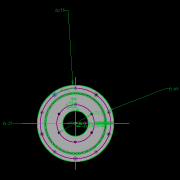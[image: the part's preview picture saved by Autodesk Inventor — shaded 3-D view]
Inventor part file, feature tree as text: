
AUTODESK INVENTOR PART (.ipt)
format: ipt  version: 2022.2 (Build 262287010, 287A)  size: 1,472,512 bytes
history: native  units: mm
features: extrude x26, other x19, sketch x16, pattern_circular x10, plane x4, fillet x2, move_body x2, revolve x2, draft x2, chamfer x2
ambient origin geometry x8: Origin, YZ Plane, XZ Plane, XY Plane, X Axis, Y Axis, Z Axis, Center Point
bodies: Solid5 (feature_tree)
feature tree (85):
  other  "CrossSection1"
  sketch  "Sketch7"  dims[d167=8.972256mm]
  other  "Roller1"
  other  "Roller2"
  sketch  "Sketch22"  dims[d173=10.814812mm]
  sketch  "Sketch2"  dims[d57=4.025mm d90=61.984365mm]
  sketch  "Sketch23"  dims[d201=75.0mm d232=0.0mm d233=3600.0mm]
  other  "RevRoller1"
  fillet  "Fillet1"  Radius=59.246882mm
  extrude  "Extrusion39"  Depth=61.984365mm
  pattern_circular  "Circular Pattern13"  Count=360  [1 undecoded]
  move_body  "Move Body7"
  revolve  "Revolution13"  [1 undecoded]
  fillet  "Fillet3"  Radius=0.025mm
  pattern_circular  "Circular Pattern14"  [2 undecoded]
  move_body  "Move Body6"
  revolve  "Revolution14"  [1 undecoded]
  other  "OuterRim_Top2"
  other  "OuterRim_Bottom2"
  plane  "Work Plane8"
  sketch  "Sketch49"  dims[d352=0.025mm]
  sketch  "Sketch50"  dims[d354=0.025mm]
  sketch  "Sketch51"  dims[d355=16.1595mm]
  extrude  "Extrusion40"  TaperAngle=360.0deg  [1 undecoded]
  extrude  "Extrusion41"  Depth=0.5mm
  extrude  "Extrusion42"  Depth=0.5mm
  extrude  "Extrusion43"  Depth=0.5mm
  sketch  "Sketch52"  dims[d356=16.159664mm]
  extrude  "Extrusion44"  Depth=1.0mm
  extrude  "Extrusion45"  Depth=0.5mm
  extrude  "Extrusion46"  TaperAngle=90.0deg  [1 undecoded]
  extrude  "Extrusion47"  Depth=0.5mm
  pattern_circular  "Circular Pattern32"  Count=24  [1 undecoded]
  pattern_circular  "Circular Pattern33"  Angle=360.0deg  [1 undecoded]
  sketch  "Sketch57"  dims[d358=360.0deg d359=0.5mm d360=240.0mm d361=360.0deg d363=1.308997mm d367=8.1mm d370=0.025mm d371=1.0mm d372=1.308997mm d373=90.0deg d374=0.5mm d375=240.0mm d376=360.0deg d378=90.0deg d379=0.1mm d380=0.025mm d381=0.025mm d382=0.025mm d383=0.025mm d384=11.193516mm d385=0.0mm d386=0.0mm d391=25.0mm d392=75.0mm d393=1.5mm d394=1.5mm d395=1.5mm d396=1.5mm d397=90.0deg d398=90.0deg d399=90.0deg d400=75.0mm d401=11.193516mm d402=0.0mm d486=0.436332mm d487=0.5mm d488=2.0mm d489=0.0mm d490=20.0mm d495=2.5mm d496=8.0mm d506=13.856406mm d507=55.5mm d508=8.0mm d509=0.05mm d510=2.5mm d511=30.0deg d512=12.0mm d513=6.0mm d514=0.2mm d515=30.0deg d516=131.0mm d517=65.5mm d518=0.2mm d519=100.0mm d520=120.0mm d521=2.0mm d522=150.0mm d530=50.0mm d531=5.5mm d532=5.5mm d533=5.5mm d534=85.75mm d535=73.5mm d536=61.25mm d537=24.5mm d538=3.0mm d539=2.4mm d540=0.0mm d541=0.0mm d542=0.0mm d543=5.5mm d544=3.0mm d545=0.0mm d546=90.0mm d547=360.0deg d549=3.0mm d550=3.0mm d551=2.4mm d552=0.0mm d553=5.596758mm d554=0.0mm d555=2.4mm d556=0.0mm d557=5.596758mm d558=0.0mm d559=5.596758mm d560=0.0mm d561=90.0mm d562=360.0deg d564=60.0mm d565=360.0deg d567=5.5mm d568=5.5mm d569=3.0mm d570=0.0mm d571=5.596758mm d572=0.0mm d573=3.0mm d574=0.0mm d575=5.596758mm d576=0.0mm d577=90.0mm d578=360.0deg d580=60.0mm d581=360.0deg d584=20.0mm d585=8.0mm d587=1.75mm d589=3.0mm d592=2.0mm d593=12.0mm d594=12.0mm d600=0.5mm d601=2.0mm d602=45.0deg d603=0.5mm d604=2.0mm d605=45.0deg d606=0.436332mm d607=0.5mm d608=0.0mm d609=20.0mm d611=360.0deg d613=0.0mm d614=0.0mm d617=0.99971mm d618=100.0mm d620=69.0mm d621=5.0mm d622=0.5mm d623=0.5mm d624=5.0mm d625=0.2mm d626=0.0mm d627=20.0mm d629=69.0mm d630=73.5mm d631=20.0mm d633=6.283185mm d635=5.5mm d636=3.0mm d637=7.0mm d638=4.0mm d639=5.596758mm d640=0.0mm d641=3.0mm d642=0.0mm d643=5.596758mm d644=0.0mm d645=4.0mm d646=0.0mm d647=20.0mm d649=6.283185mm d651=3.0mm d652=4.0mm d653=20.0mm d655=6.283185mm d657=7.0mm d658=5.5mm d659=5.596758mm d660=0.0mm d661=2.593516mm d662=0.0mm d663=5.596758mm d664=0.0mm d665=3.193516mm d666=0.0mm d679=50.0mm d680=360.0deg d682=50.0mm d683=360.0deg d694=6.35mm d695=6.35mm d696=6.0mm d697=6.0mm d698=11.194mm d699=0.0mm d700=8.194mm d701=0.0mm d702=60.0mm d703=360.0deg d705=4.8mm d16=0.872665mm d17=0.872665mm d49=0.872665mm d50=0.872665mm d51=0.872665mm d52=0.872665mm d236=0.5mm d237=0.872665mm d238=0.5mm d239=0.872665mm d282=1.0mm d283=1.0mm d284=1.0mm d285=0.15mm d286=0.25mm d287=0.375mm d288=14.3117mm d289=0.75mm d290=20.594885mm d291=0.0625mm d292=0.75mm d293=0.375mm d405=0.5mm d406=0.872665mm d407=0.5mm d408=0.872665mm d413=0.5mm d414=0.872665mm d415=0.5mm d416=0.872665mm d417=0.5mm d418=0.872665mm d419=0.5mm d420=0.872665mm d421=0.872665mm d431=0.5mm d432=0.872665mm d433=0.5mm d434=0.872665mm d471=0.5mm d472=0.872665mm d473=0.5mm d474=0.872665mm d497=0.5mm d498=0.872665mm d499=0.5mm d500=0.872665mm d590=0.5mm d591=0.872665mm]
  extrude  "Extrusion50"  TaperAngle=90.0deg  [1 undecoded]
  extrude  "Extrusion51"  Depth=0.1mm
  pattern_circular  "Circular Pattern34"  [2 undecoded]
  plane  "Work Plane7"
  sketch  "Sketch47"  dims[d350=47.575427mm]
  extrude  "Rotor_Ring"  Depth=0.5mm
  draft  "FaceDraft2"
  sketch  "Sketch30"  dims[d343=16.1595mm d344=16.159664mm d345=0.025mm]
  plane  "Work Plane5"
  other  "Rotor Featurs"
  other  "RotorRim_Bottom"
  extrude  "Extrusion24"  Depth=0.5mm
  extrude  "Extrusion25"  Depth=0.5mm
  extrude  "Extrusion26"  Depth=11.193516mm
  pattern_circular  "Circular Pattern23"  [2 undecoded]
  sketch  "Sketch41"  dims[d347=0.1mm]
  extrude  "Extrusion27"  TaperAngle=0.0deg  [1 undecoded]
  extrude  "Extrusion28"  Depth=25.0mm
  pattern_circular  "Circular Pattern24"  [2 undecoded]
  extrude  "Extrusion29"  Depth=1.5mm
  extrude  "Extrusion30"  Depth=1.5mm
  extrude  "Extrusion31"  Depth=1.5mm
  pattern_circular  "Circular Pattern25"  [2 undecoded]
  sketch  "Sketch42"  dims[d348=0.1mm]
  extrude  "Extrusion32"  TaperAngle=90.0deg  [1 undecoded]
  extrude  "Extrusion33"  TaperAngle=90.0deg  [1 undecoded]
  extrude  "Extrusion34"  TaperAngle=90.0deg  [1 undecoded]
  extrude  "Extrusion35"  Depth=0.5mm
  pattern_circular  "Circular Pattern26"  [2 undecoded]
  pattern_circular  "Circular Pattern27"  [2 undecoded]
  chamfer  "Chamfer1"  Distance=0.436332mm
  chamfer  "Chamfer2"  Distance=0.5mm
  draft  "FaceDraft4"
  plane  "Work Plane6"
  sketch  "Sketch43"  dims[d349=47.575591mm]
  extrude  "Extrusion37"  Depth=0.5mm
  extrude  "Extrusion38"  Depth=8.0mm
  other  "2D Equation Curve1"
  sketch  "Sketch40"  dims[d346=0.025mm]
  other  "Work Axis6"
  other  "Work Axis7"
  other  "Work Axis8"
  other  "Work Axis9"
  other  "Work Axis10"
  other  "Work Point1"
  other  "Work Point2"
  other  "Work Point3"
  other  "Work Point4"
  other  "Work Point5"
  sketch  "Sketch48"  dims[d351=0.025mm]
note: 26 required parameter values undecoded (feature->parameter linkage not recoverable at this tier; creation-order binding heuristic only, values carry confidence <= 0.55)